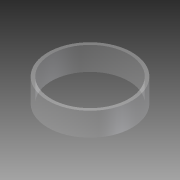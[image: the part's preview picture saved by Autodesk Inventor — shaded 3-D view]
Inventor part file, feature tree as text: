
AUTODESK INVENTOR PART (.ipt)
format: ipt  version: 2012 (Build 160160000, 160)  size: 78,336 bytes
history: native  units: mm
features: extrude x1, sketch x1
ambient origin geometry x8: Origin, YZ Plane, XZ Plane, XY Plane, X Axis, Y Axis, Z Axis, Center Point
bodies: Solid1 (feature_tree)
feature tree (2):
  extrude  "Extrusion1"  Depth=82.55mm
  sketch  "Sketch1"  dims[d0=76.2mm d1=82.55mm d2=23.0mm d3=0.0mm]
